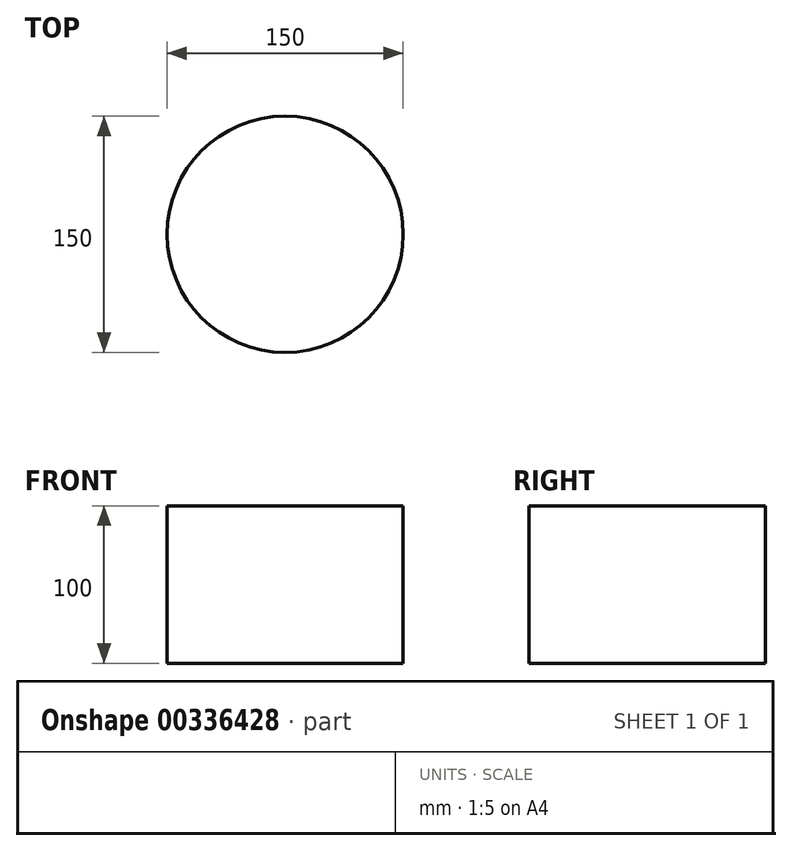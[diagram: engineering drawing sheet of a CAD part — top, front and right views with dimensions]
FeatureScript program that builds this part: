
annotation { "Feature Type Name" : "Feature", "Feature Type Description" : "" }
export const myFeature = defineFeature(function(context is Context, id is Id, definition is map)
    precondition{}
    {
        {
            var Q0;
            Q0=qCreatedBy(makeId("Top.planeOp"),FACE);
            var sketch = newSketch(context, id + "F0", { "sketchPlane" : qUnion([Q0])});
            skCircle(sketch, "E0", {"center": v(0.47, -0.6) * mm, "radius": 75 * mm});
            skPoint(sketch, "E0.first.point", {"position": v(-46.13, -59.36) * mm});
            skPoint(sketch, "E0.second.point", {"position": v(-67.03, 32.1) * mm});
            skPoint(sketch, "E0.third.point", {"position": v(57.37, 48.27) * mm});
            skPoint(sketch, "E1.0", {"position": v(0, 0) * mm});
            skSolve(sketch);
        }
        {
            var Q0;
            Q0=makeQuery(id+"F0.imprint","IMPRINT",FACE,{"disambiguationData":[TD([[makeQuery(id+"F0.imprint","IMPRINT",EDGE,{"derivedFrom":sQuery(id+"F0.wireOp",EDGE,"E0")}),1.0]])]});
            extrude(context, id + "F1", {"entities" : qUnion([Q0]), "depth" : 100 * mm});
        }
    });
